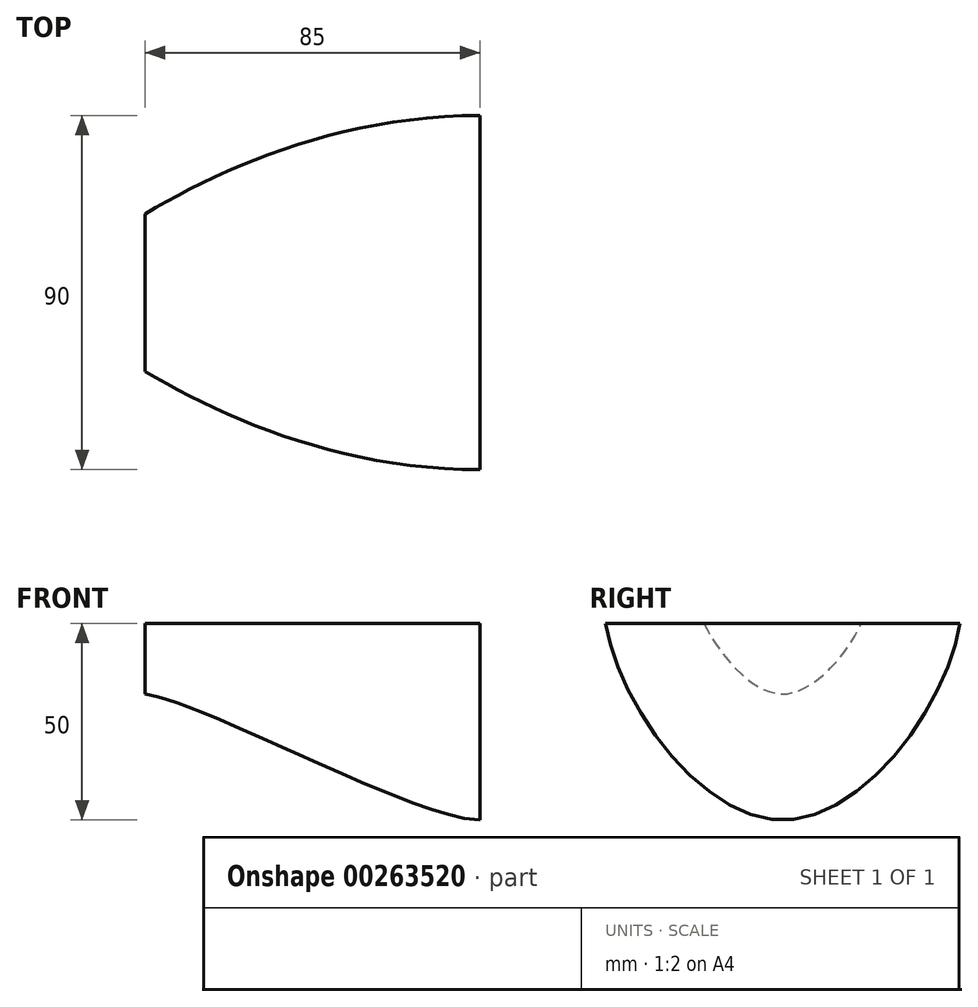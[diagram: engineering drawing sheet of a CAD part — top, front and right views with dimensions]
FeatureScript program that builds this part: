
annotation { "Feature Type Name" : "Feature", "Feature Type Description" : "" }
export const myFeature = defineFeature(function(context is Context, id is Id, definition is map)
    precondition{}
    {
        {
            var Q0;
            Q0=qCreatedBy(makeId("Right.planeOp"),FACE);
            cPlane(context, id + "F0", {"entities" : qUnion([Q0]), "cplaneType" : CPlaneType.OFFSET, "offset" : 85 * mm, "oppositeDirection" : true, "width" : 150 * mm, "height" : 150 * mm});
        }
        {
            var Q0;
            Q0=qCreatedBy(makeId("Right.planeOp"),FACE);
            var sketch = newSketch(context, id + "F1", { "sketchPlane" : qUnion([Q0])});
            skFitSpline(sketch, "E0", {"points": [v(-45, 0) * mm, v(0, -50) * mm, v(45, 0) * mm], "startDerivative": vector(18, -120) * mm, "endDerivative": vector(18, 120) * mm});
            skLineSegment(sketch, "E1", {"start": v(-45, 0) * mm, "end": v(45, 0) * mm});
            skSolve(sketch);
        }
        {
            var Q0;
            Q0=qCreatedBy(id+"F0.planeOp",FACE);
            var sketch = newSketch(context, id + "F2", { "sketchPlane" : qUnion([Q0])});
            skFitSpline(sketch, "E2", {"points": [v(-20, 0) * mm, v(0, -18) * mm, v(20, 0) * mm], "startDerivative": vector(12, -30) * mm, "endDerivative": vector(12, 30) * mm});
            skLineSegment(sketch, "E3", {"start": v(-20, 0) * mm, "end": v(20, 0) * mm});
            skSolve(sketch);
        }
        {
            var Q0;
            Q0=qCreatedBy(makeId("Top.planeOp"),FACE);
            var sketch = newSketch(context, id + "F3", { "sketchPlane" : qUnion([Q0])});
            skFitSpline(sketch, "E4", {"points": [v(-85, 20) * mm, v(0, 45) * mm], "startDerivative": vector(60, 36) * mm, "endDerivative": vector(105, 0) * mm});
            skFitSpline(sketch, "E5", {"points": [v(-85, -20) * mm, v(0, -45) * mm], "startDerivative": vector(60, -36) * mm, "endDerivative": vector(105, 0) * mm});
            skSolve(sketch);
        }
        {
            var Q0;
            Q0=qCreatedBy(makeId("Front.planeOp"),FACE);
            var sketch = newSketch(context, id + "F4", { "sketchPlane" : qUnion([Q0])});
            skFitSpline(sketch, "E6", {"points": [v(-85, -18) * mm, v(0, -50) * mm], "startDerivative": vector(45, -6) * mm, "endDerivative": vector(48.05, 0) * mm});
            skSolve(sketch);
        }
        {
            var Q0;
            Q0=makeQuery(id+"F2.imprint","IMPRINT",FACE,{"disambiguationData":[TD([[makeQuery(id+"F2.imprint","IMPRINT",EDGE,{"derivedFrom":sQuery(id+"F2.wireOp",EDGE,"E2")}),1.0]])]});
            var Q1;
            Q1=makeQuery(id+"F1.imprint","IMPRINT",FACE,{"disambiguationData":[TD([[makeQuery(id+"F1.imprint","IMPRINT",EDGE,{"derivedFrom":sQuery(id+"F1.wireOp",EDGE,"E0")}),1.0]])]});
            var Q2;
            Q2=sQuery(id+"F3.wireOp",EDGE,"E5");
            var Q3;
            Q3=sQuery(id+"F3.wireOp",EDGE,"E4");
            var Q4;
            Q4=sQuery(id+"F4.wireOp",EDGE,"E6");
            loft(context, id + "F5", {"addGuides" : true, "sheetProfilesArray" : [{ "sheetProfileEntities" : qUnion([Q0]) }, { "sheetProfileEntities" : qUnion([Q1]) }], "guidesArray" : [{ "guideEntities" : qUnion([Q2]), "guideDerivativeType" : LoftGuideDerivativeType.DEFAULT, "guideDerivativeMagnitude" : 1 }, { "guideEntities" : qUnion([Q3]), "guideDerivativeType" : LoftGuideDerivativeType.DEFAULT, "guideDerivativeMagnitude" : 1 }, { "guideEntities" : qUnion([Q4]), "guideDerivativeType" : LoftGuideDerivativeType.DEFAULT, "guideDerivativeMagnitude" : 1 }]});
        }
    });
